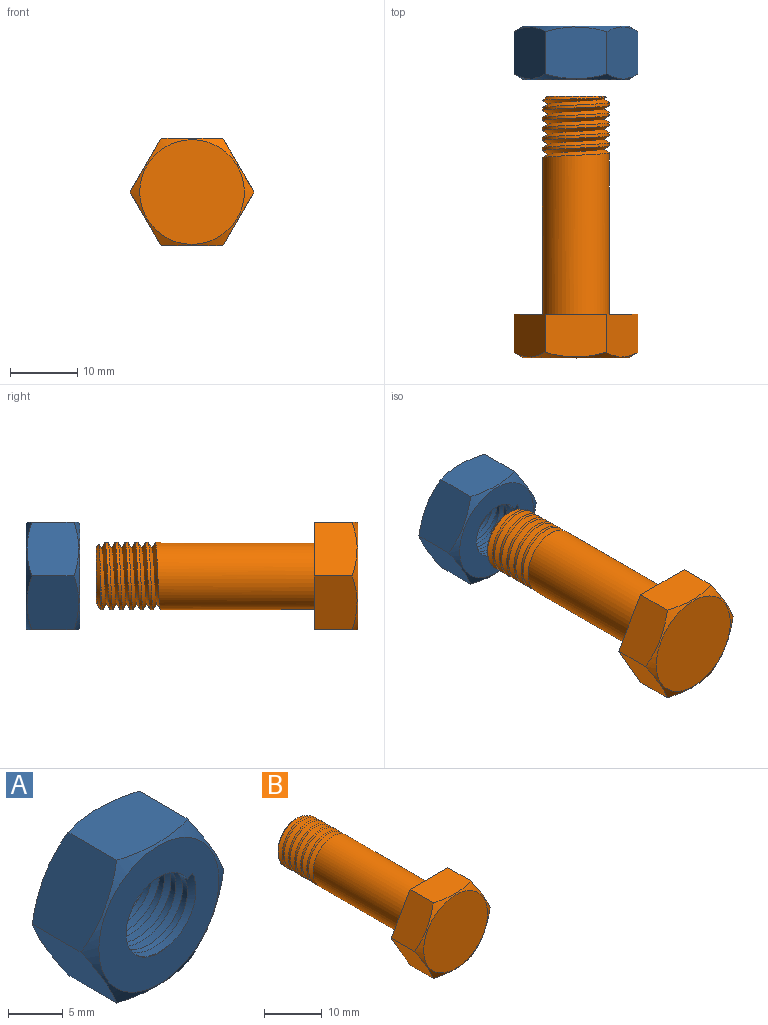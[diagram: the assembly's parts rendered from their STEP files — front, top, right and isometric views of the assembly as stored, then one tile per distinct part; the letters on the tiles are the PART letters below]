
ASSEMBLY  parts=2 mates=2
PART A: 15 faces, bbox 18.8x9.2x18.8 mm
  f0: plane 15.91x15.91mm, normal (0,-1,0), area 130.1mm2, adj f1,f10,f13,f14
  f1: cylinder r=4.25mm len=8.5mm, axis (0,-1,0), area 94.4mm2, adj f0,f2,f11,f12,f13,f14
  f2: plane 15.91x15.91mm, normal (0,1,0), area 130.1mm2, adj f1,f3,f11,f12
  f3: cone r=7.77mm half-angle=60deg, axis (0,-1,0), area 36.8mm2, adj f2,f4,f5,f6,f7,f8,f9
  f4: plane 9.24x7.74mm, normal (0,0,-1), area 67mm2, adj f3,f7,f9,f10
  f5: plane 8x7.75mm, normal (-0.87,0,0.5), area 67mm2, adj f3,f7,f8,f10
  f6: plane 8x7.75mm, normal (0.87,0,0.5), area 67mm2, adj f3,f8,f9,f10
  f7: plane 8x7.75mm, normal (-0.87,0,-0.5), area 67mm2, adj f3,f4,f5,f10
  f8: plane 9.25x7.74mm, normal (0,0,1), area 67mm2, adj f3,f5,f6,f10
  f9: plane 8x7.75mm, normal (0.87,0,-0.5), area 67mm2, adj f3,f4,f6,f10
  f10: cone r=7.77mm half-angle=60deg, axis (0,1,0), area 36.8mm2, adj f0,f4,f5,f6,f7,f8,f9
  f11: plane 0.75x0.43mm, normal (1,0,0), area 0.2mm2, adj f1,f2,f14
  f12: bspline ~11.55x10mm, area 131mm2, adj f1,f2,f13,f14
  f13: plane 0.65x0.43mm, normal (0.5,0,-0.87), area 0.2mm2, adj f0,f1,f12
  f14: bspline ~11.55x10mm, area 130.9mm2, adj f0,f1,f11,f12
PART B: 21 faces, bbox 18.6x39.9x18.6 mm
  f0: cylinder r=5mm len=24.47mm, axis (0,-1,0), area 736.2mm2, adj f6,f7,f18,f19,f20
  f1: cylinder r=5mm len=5mm, axis (0,-1,0), area 1.4mm2, adj f2,f11,f19
  f2: cylinder r=5mm len=10mm, axis (0,-1,0), area 13.7mm2, adj f1,f3,f11,f19,f20
  f3: cylinder r=5mm len=10mm, axis (0,-1,0), area 13.7mm2, adj f2,f4,f19,f20
  f4: cylinder r=5mm len=10mm, axis (0,-1,0), area 13.7mm2, adj f3,f5,f19,f20
  f5: cylinder r=5mm len=10mm, axis (0,-1,0), area 13.7mm2, adj f4,f6,f19,f20
  f6: cylinder r=5mm len=10mm, axis (0,-1,0), area 13.7mm2, adj f0,f5,f19,f20
  f7: plane 18.48x16mm, normal (0,1,0), area 143.2mm2, adj f0,f12,f13,f14,f15,f16,f17
  f8: cone r=7.8mm half-angle=60deg, axis (0,1,0), area 35.3mm2, adj f9,f12,f13,f14,f15,f16,f17
  f9: plane 15.6x15.6mm, normal (0,-1,0), area 191.1mm2, adj f8
  f10: plane 8.92x8.62mm, normal (0,1,0), area 59.8mm2, adj f11,f19,f20
  f11: cone r=5mm half-angle=45deg, axis (0,-1,0), area 13mm2, adj f1,f2,f10,f19,f20
  f12: plane 9.25x6.39mm, normal (0,0,1), area 56.7mm2, adj f7,f8,f15,f17
  f13: plane 8x6.39mm, normal (-0.87,0,-0.5), area 56.7mm2, adj f7,f8,f15,f16
  f14: plane 8x6.39mm, normal (0.87,0,-0.5), area 56.7mm2, adj f7,f8,f16,f17
  f15: plane 8x6.39mm, normal (-0.87,0,0.5), area 56.7mm2, adj f7,f8,f12,f13
  f16: plane 9.25x6.39mm, normal (0,0,-1), area 56.7mm2, adj f7,f8,f13,f14
  f17: plane 8x6.39mm, normal (0.87,0,0.5), area 56.7mm2, adj f7,f8,f12,f14
  f18: plane 1.06x0.92mm, normal (0.1,0,-0.99), area 0.5mm2, adj f0,f19,f20
  f19: bspline ~11.55x10.28mm, area 180.4mm2, adj f0,f1,f2,f3,f4,f5,f6,f10
  f20: bspline ~11.55x10.28mm, area 191.4mm2, adj f0,f2,f3,f4,f5,f6,f10,f11
PLACE A t=(-13.93,12.68,6.18)mm
PLACE B t=(-13.93,-26.37,6.18)mm
MATE planar A.f0 <-> B.f11  axis (0,-1,0) through (-14.03,8.63,6.18)mm
MATE slider B.f8 <-> A.f1  axis (0,1,0) through (-13.93,6.13,6.18)mm
